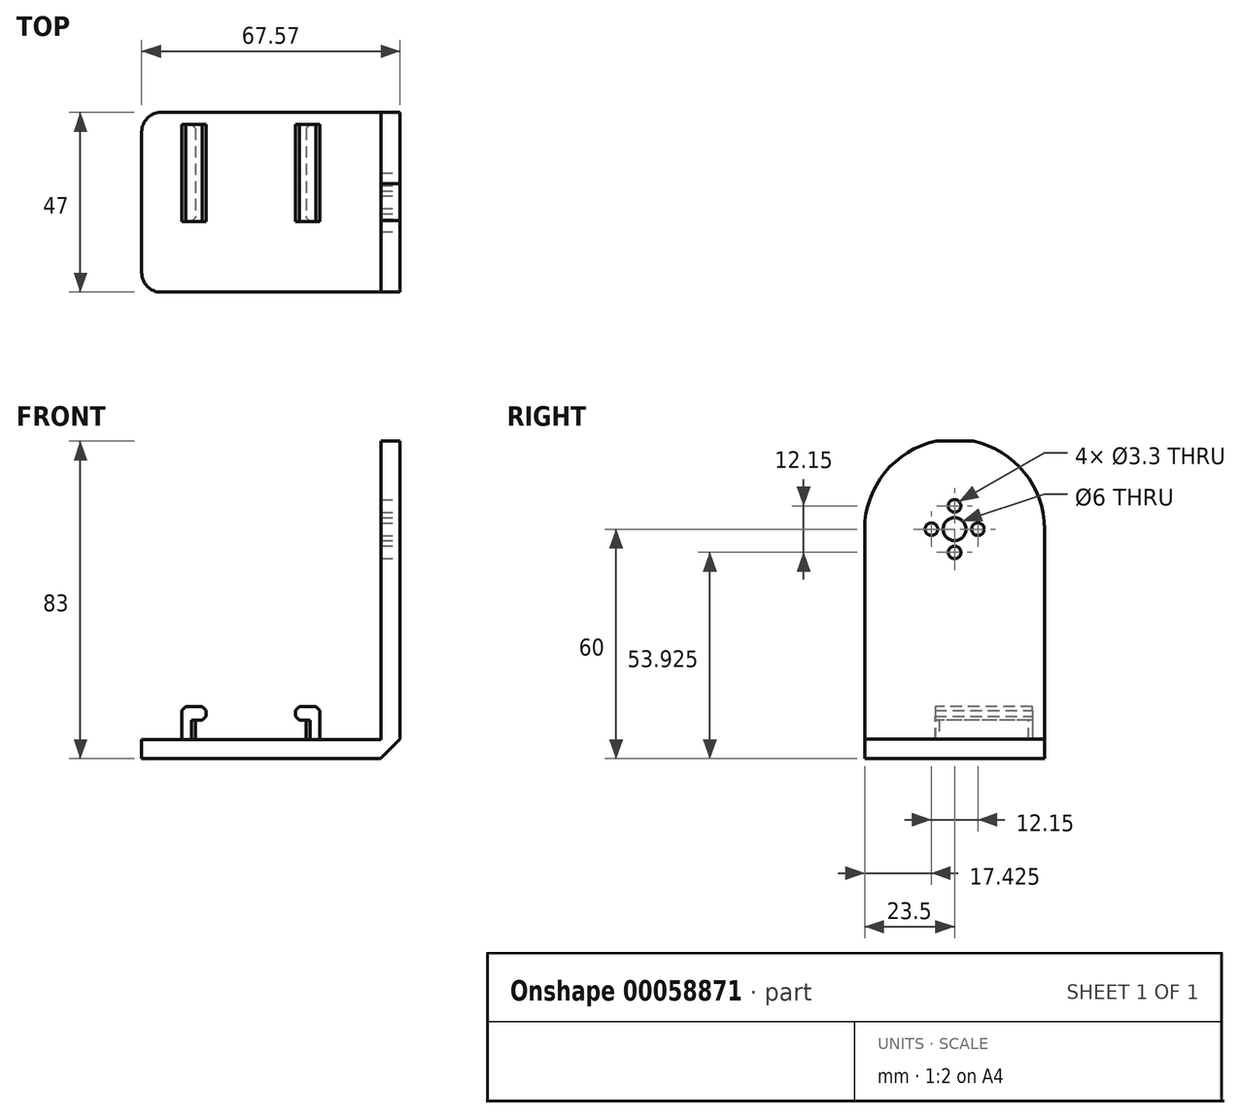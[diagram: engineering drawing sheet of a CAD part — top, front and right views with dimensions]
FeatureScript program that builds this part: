
annotation { "Feature Type Name" : "Feature", "Feature Type Description" : "" }
export const myFeature = defineFeature(function(context is Context, id is Id, definition is map)
    precondition{}
    {
        {
            var Q0;
            Q0=qCreatedBy(makeId("Top.planeOp"),FACE);
            var sketch = newSketch(context, id + "F0", { "sketchPlane" : qUnion([Q0])});
            skLineSegment(sketch, "E0.bottom", {"start": v(-28.58, 10.8) * mm, "end": v(28.58, 10.8) * mm});
            skLineSegment(sketch, "E0.top", {"start": v(-28.58, -10.8) * mm, "end": v(28.58, -10.8) * mm});
            skLineSegment(sketch, "E0.left", {"start": v(-28.57, 10.8) * mm, "end": v(-28.58, -10.8) * mm});
            skLineSegment(sketch, "E0.right", {"start": v(28.58, 10.8) * mm, "end": v(28.57, -10.8) * mm});
            skLineSegment(sketch, "E1", {"start": v(0, 10.8) * mm, "end": v(0, -10.8) * mm, "construction": true});
            skPoint(sketch, "E2", {"position": v(0, 0) * mm});
            skSolve(sketch);
        }
        {
            var Q0;
            Q0=qSketchRegion(id+"F0",true);
            extrude(context, id + "F1", {"entities" : qUnion([Q0]), "depth" : 5 * mm});
        }
        {
            var Q0;
            Q0=qCreatedBy(makeId("Top.planeOp"),FACE);
            var sketch = newSketch(context, id + "F2", { "sketchPlane" : qUnion([Q0])});
            skLineSegment(sketch, "E3.bottom", {"start": v(-28.57, 10.8) * mm, "end": v(28.58, 10.8) * mm});
            skLineSegment(sketch, "E3.top", {"start": v(-28.57, 36.2) * mm, "end": v(28.58, 36.2) * mm});
            skLineSegment(sketch, "E3.left", {"start": v(-28.57, 10.8) * mm, "end": v(-28.58, 36.2) * mm});
            skLineSegment(sketch, "E3.right", {"start": v(28.58, 10.8) * mm, "end": v(28.58, 36.2) * mm});
            skSolve(sketch);
        }
        {
            var Q0;
            Q0=qSketchRegion(id+"F2",true);
            extrude(context, id + "F3", {"entities" : qUnion([Q0]), "operationType" : NewBodyOperationType.ADD, "depth" : 5 * mm});
        }
        {
            var Q0;
            Q0=makeQuery(id+"F3.boolean.opBoolean","MERGE",FACE,{"derivedFrom":[makeQuery(id+"F1.opExtrude","CAP_FACE",FACE,{"disambiguationData":[OSD([sQuery(id+"F0.wireOp",EDGE,"E0.bottom"),sQuery(id+"F0.wireOp",EDGE,"E0.top"),sQuery(id+"F0.wireOp",EDGE,"E0.left"),sQuery(id+"F0.wireOp",EDGE,"E0.right"),sQuery(id+"F0.wireOp",EDGE,"28a9c39b-f770-489b-a02f-ce0b1f26b331"),sQuery(id+"F0.wireOp",EDGE,"4d5f723c-dec2-4723-b848-b3ff6702b9b40.MirrorC"),sQuery(id+"F0.wireOp",EDGE,"3c9fb506-c623-4861-a3c0-1a61a185bb210.MirrorC"),sQuery(id+"F0.wireOp",EDGE,"cd34c67d-a8e0-44d2-8d65-12e7f07ee4970.MirrorC")])],"isStart":false}),makeQuery(id+"F3.opExtrude","CAP_FACE",FACE,{"disambiguationData":[OSD([sQuery(id+"F2.wireOp",EDGE,"E3.bottom"),sQuery(id+"F2.wireOp",EDGE,"E3.top"),sQuery(id+"F2.wireOp",EDGE,"E3.left"),sQuery(id+"F2.wireOp",EDGE,"E3.right")])],"isStart":false})]});
            var sketch = newSketch(context, id + "F4", { "sketchPlane" : qUnion([Q0])});
            skLineSegment(sketch, "E4.bottom", {"start": v(-18.03, 33.02) * mm, "end": v(-14.48, 33.02) * mm});
            skLineSegment(sketch, "E4.top", {"start": v(-18.03, 7.62) * mm, "end": v(-14.48, 7.62) * mm});
            skLineSegment(sketch, "E4.left", {"start": v(-18.03, 33.02) * mm, "end": v(-18.03, 7.62) * mm});
            skLineSegment(sketch, "E4.right", {"start": v(-14.48, 33.02) * mm, "end": v(-14.48, 7.62) * mm});
            skLineSegment(sketch, "E5.MirrorCS", {"start": v(18.03, 7.62) * mm, "end": v(14.48, 7.62) * mm});
            skLineSegment(sketch, "E6.MirrorCS", {"start": v(14.48, 33.02) * mm, "end": v(14.48, 7.62) * mm});
            skLineSegment(sketch, "E7.MirrorCS", {"start": v(18.03, 33.02) * mm, "end": v(14.48, 33.02) * mm});
            skLineSegment(sketch, "E8.MirrorCS", {"start": v(18.03, 33.02) * mm, "end": v(18.03, 7.62) * mm});
            skLineSegment(sketch, "E9", {"start": v(-28.58, 12.7) * mm, "end": v(28.58, 12.7) * mm, "construction": true});
            skLineSegment(sketch, "E10", {"start": v(28.58, 20.32) * mm, "end": v(-28.57, 20.32) * mm, "construction": true});
            skPoint(sketch, "E11", {"position": v(-18.03, 20.32) * mm});
            skSolve(sketch);
        }
        {
            var Q0;
            Q0=qSketchRegion(id+"F4",true);
            extrude(context, id + "F5", {"entities" : qUnion([Q0]), "operationType" : NewBodyOperationType.ADD, "depth" : 5.08 * mm});
        }
        {
            var Q0;
            Q0=makeQuery(id+"F5.opExtrude","CAP_FACE",FACE,{"disambiguationData":[OSD([sQuery(id+"F4.wireOp",EDGE,"E4.bottom"),sQuery(id+"F4.wireOp",EDGE,"E4.top"),sQuery(id+"F4.wireOp",EDGE,"E4.left"),sQuery(id+"F4.wireOp",EDGE,"E4.right")])],"isStart":false});
            var sketch = newSketch(context, id + "F6", { "sketchPlane" : qUnion([Q0])});
            skLineSegment(sketch, "E12.bottom", {"start": v(-18.03, 33.02) * mm, "end": v(-11.68, 33.02) * mm});
            skLineSegment(sketch, "E12.top", {"start": v(-18.03, 7.62) * mm, "end": v(-11.68, 7.62) * mm});
            skLineSegment(sketch, "E12.left", {"start": v(-18.03, 33.02) * mm, "end": v(-18.03, 7.62) * mm});
            skLineSegment(sketch, "E12.right", {"start": v(-11.68, 33.02) * mm, "end": v(-11.68, 7.62) * mm});
            skLineSegment(sketch, "E13.bottom", {"start": v(18.03, 33.02) * mm, "end": v(11.68, 33.02) * mm});
            skLineSegment(sketch, "E13.top", {"start": v(18.03, 7.62) * mm, "end": v(11.68, 7.62) * mm});
            skLineSegment(sketch, "E13.left", {"start": v(18.03, 33.02) * mm, "end": v(18.03, 7.62) * mm});
            skLineSegment(sketch, "E13.right", {"start": v(11.68, 33.02) * mm, "end": v(11.68, 7.62) * mm});
            skSolve(sketch);
        }
        {
            var Q0;
            Q0=qSketchRegion(id+"F6",true);
            extrude(context, id + "F7", {"entities" : qUnion([Q0]), "operationType" : NewBodyOperationType.ADD, "depth" : 3.56 * mm});
        }
        {
            var Q0;
            Q0=makeQuery(id+"F7.opExtrude","CAP_EDGE",EDGE,{"disambiguationData":[OSD([sQuery(id+"F6.wireOp",EDGE,"E12.right")])],"isStart":false});
            var Q1;
            Q1=makeQuery(id+"F7.opExtrude","CAP_EDGE",EDGE,{"disambiguationData":[OSD([sQuery(id+"F6.wireOp",EDGE,"E12.right")])],"isStart":true});
            var Q2;
            Q2=makeQuery(id+"F7.opExtrude","CAP_EDGE",EDGE,{"disambiguationData":[OSD([sQuery(id+"F6.wireOp",EDGE,"E13.right")])],"isStart":false});
            var Q3;
            Q3=makeQuery(id+"F7.opExtrude","CAP_EDGE",EDGE,{"disambiguationData":[OSD([sQuery(id+"F6.wireOp",EDGE,"E13.right")])],"isStart":true});
            var Q4;
            Q4=makeQuery(id+"F7.opExtrude","CAP_EDGE",EDGE,{"disambiguationData":[OSD([sQuery(id+"F6.wireOp",EDGE,"E13.left")])],"isStart":false});
            var Q5;
            Q5=makeQuery(id+"F7.opExtrude","CAP_EDGE",EDGE,{"disambiguationData":[OSD([sQuery(id+"F6.wireOp",EDGE,"E12.left")])],"isStart":false});
            var Q6;
            Q6=makeQuery(id+"F5.opExtrude","CAP_EDGE",EDGE,{"disambiguationData":[OSD([sQuery(id+"F4.wireOp",EDGE,"E8.MirrorCS")])],"isStart":true});
            var Q7;
            Q7=makeQuery(id+"F5.opExtrude","CAP_EDGE",EDGE,{"disambiguationData":[OSD([sQuery(id+"F4.wireOp",EDGE,"E4.left")])],"isStart":true});
            var Q8;
            Q8=makeQuery(id+"F5.opExtrude","SWEPT_EDGE",EDGE,{"disambiguationData":[OSD([sQuery(id+"F4.wireOp",EDGE,"E6.MirrorCS"),sQuery(id+"F4.wireOp",EDGE,"E7.MirrorCS")])]});
            var Q9;
            Q9=makeQuery(id+"F5.opExtrude","SWEPT_EDGE",EDGE,{"disambiguationData":[OSD([sQuery(id+"F4.wireOp",EDGE,"E4.bottom"),sQuery(id+"F4.wireOp",EDGE,"E4.right")])]});
            var Q10;
            Q10=makeQuery(id+"F5.opExtrude","SWEPT_EDGE",EDGE,{"disambiguationData":[OSD([sQuery(id+"F4.wireOp",EDGE,"E4.top"),sQuery(id+"F4.wireOp",EDGE,"E4.right")])]});
            var Q11;
            Q11=makeQuery(id+"F5.opExtrude","SWEPT_EDGE",EDGE,{"disambiguationData":[OSD([sQuery(id+"F4.wireOp",EDGE,"E5.MirrorCS"),sQuery(id+"F4.wireOp",EDGE,"E6.MirrorCS")])]});
            chamfer(context, id + "F8", {"entities" : qUnion([Q0, Q1, Q2, Q3, Q4, Q5, Q6, Q7, Q8, Q9, Q10, Q11]), "width" : 1.02 * mm, "tangentPropagation" : true});
        }
        {
            var Q0;
            Q0=makeQuery(id+"F3.boolean.opBoolean","MERGE",FACE,{"derivedFrom":[makeQuery(id+"F1.opExtrude","CAP_FACE",FACE,{"disambiguationData":[OSD([sQuery(id+"F0.wireOp",EDGE,"E0.bottom"),sQuery(id+"F0.wireOp",EDGE,"E0.top"),sQuery(id+"F0.wireOp",EDGE,"E0.left"),sQuery(id+"F0.wireOp",EDGE,"E0.right")])],"isStart":false}),makeQuery(id+"F3.opExtrude","CAP_FACE",FACE,{"disambiguationData":[OSD([sQuery(id+"F2.wireOp",EDGE,"E3.bottom"),sQuery(id+"F2.wireOp",EDGE,"E3.top"),sQuery(id+"F2.wireOp",EDGE,"E3.left"),sQuery(id+"F2.wireOp",EDGE,"E3.right")])],"isStart":false})]});
            var sketch = newSketch(context, id + "F9", { "sketchPlane" : qUnion([Q0])});
            skLineSegment(sketch, "E14.bottom", {"start": v(28.58, -10.8) * mm, "end": v(39, -10.8) * mm});
            skLineSegment(sketch, "E14.top", {"start": v(28.58, 36.2) * mm, "end": v(39, 36.2) * mm});
            skLineSegment(sketch, "E14.left", {"start": v(28.57, -10.8) * mm, "end": v(28.57, 36.2) * mm});
            skLineSegment(sketch, "E14.right", {"start": v(39, -10.8) * mm, "end": v(39, 36.2) * mm});
            skLineSegment(sketch, "E15", {"start": v(0, -10.8) * mm, "end": v(0, 36.2) * mm, "construction": true});
            skSolve(sketch);
        }
        {
            var Q0;
            Q0 = qSketchRegion(id + "F9", true);
            extrude(context, id + "F10", {"entities" : qUnion([Q0]), "operationType" : NewBodyOperationType.ADD, "oppositeDirection" : true, "depth" : 5 * mm});
        }
        {
            var Q0;
            Q0=makeQuery(id+"F10.boolean.opBoolean","MERGE",FACE,{"derivedFrom":[makeQuery(id+"F3.boolean.opBoolean","MERGE",FACE,{"derivedFrom":[makeQuery(id+"F1.opExtrude","CAP_FACE",FACE,{"disambiguationData":[OSD([sQuery(id+"F0.wireOp",EDGE,"E0.bottom"),sQuery(id+"F0.wireOp",EDGE,"E0.top"),sQuery(id+"F0.wireOp",EDGE,"E0.left"),sQuery(id+"F0.wireOp",EDGE,"E0.right")])],"isStart":false}),makeQuery(id+"F3.opExtrude","CAP_FACE",FACE,{"disambiguationData":[OSD([sQuery(id+"F2.wireOp",EDGE,"E3.bottom"),sQuery(id+"F2.wireOp",EDGE,"E3.top"),sQuery(id+"F2.wireOp",EDGE,"E3.left"),sQuery(id+"F2.wireOp",EDGE,"E3.right")])],"isStart":false})]}),makeQuery(id+"F10.opExtrude","CAP_FACE",FACE,{"disambiguationData":[OSD([sQuery(id+"F9.wireOp",EDGE,"E14.bottom"),sQuery(id+"F9.wireOp",EDGE,"E14.top"),sQuery(id+"F9.wireOp",EDGE,"E14.left"),sQuery(id+"F9.wireOp",EDGE,"E14.right")])],"isStart":true})]});
            var sketch = newSketch(context, id + "F11", { "sketchPlane" : qUnion([Q0])});
            skLineSegment(sketch, "E16.bottom", {"start": v(39, -10.8) * mm, "end": v(34, -10.8) * mm});
            skLineSegment(sketch, "E16.top", {"start": v(39, 36.2) * mm, "end": v(34, 36.2) * mm});
            skLineSegment(sketch, "E16.left", {"start": v(39, -10.8) * mm, "end": v(39, 36.2) * mm});
            skLineSegment(sketch, "E16.right", {"start": v(34, -10.8) * mm, "end": v(34, 36.2) * mm});
            skSolve(sketch);
        }
        {
            var Q0;
            Q0 = qSketchRegion(id + "F11", true);
            extrude(context, id + "F12", {"entities" : qUnion([Q0]), "operationType" : NewBodyOperationType.ADD, "depth" : 78 * mm});
        }
        {
            var Q0;
            Q0=makeQuery(id+"F12.boolean.opBoolean","MERGE",FACE,{"derivedFrom":[makeQuery(id+"F10.opExtrude","SWEPT_FACE",FACE,{"disambiguationData":[OSD([sQuery(id+"F9.wireOp",EDGE,"E14.right")])]}),makeQuery(id+"F12.opExtrude","SWEPT_FACE",FACE,{"disambiguationData":[OSD([sQuery(id+"F11.wireOp",EDGE,"E16.left")])]})]});
            var sketch = newSketch(context, id + "F13", { "sketchPlane" : qUnion([Q0])});
            skLineSegment(sketch, "E17", {"start": v(12.7, 83) * mm, "end": v(12.7, 0) * mm, "construction": true});
            skLineSegment(sketch, "E18", {"start": v(-10.8, 60) * mm, "end": v(36.2, 60) * mm, "construction": true});
            skCircle(sketch, "E19", {"center": v(6.62, 60) * mm, "radius": 1.65 * mm});
            skCircle(sketch, "E20", {"center": v(12.7, 53.92) * mm, "radius": 1.65 * mm});
            skCircle(sketch, "E21.MirrorC", {"center": v(18.77, 60) * mm, "radius": 1.65 * mm});
            skCircle(sketch, "E22.MirrorC", {"center": v(12.7, 66.07) * mm, "radius": 1.65 * mm});
            skCircle(sketch, "E23", {"center": v(12.7, 60) * mm, "radius": 3 * mm});
            skSolve(sketch);
        }
        {
            var Q0;
            Q0 = qSketchRegion(id + "F13", true);
            extrude(context, id + "F14", {"entities" : qUnion([Q0]), "operationType" : NewBodyOperationType.REMOVE, "oppositeDirection" : true, "depth" : 25.4 * mm});
        }
        {
            var Q0;
            Q0=makeQuery(id+"F12.opExtrude","SWEPT_FACE",FACE,{"disambiguationData":[OSD([sQuery(id+"F11.wireOp",EDGE,"E16.right")])]});
            var sketch = newSketch(context, id + "F15", { "sketchPlane" : qUnion([Q0])});
            skArc(sketch, "E24", {"start": v(10.8, 60) * mm, "mid": v(-12.7, 83.5) * mm, "end": v(-36.2, 60) * mm});
            skLineSegment(sketch, "E25", {"start": v(-36.2, 60) * mm, "end": v(10.8, 60) * mm, "construction": true});
            skLineSegment(sketch, "E26", {"start": v(-36.2, 60) * mm, "end": v(-36.2, 83) * mm});
            skLineSegment(sketch, "E27", {"start": v(-36.2, 83) * mm, "end": v(10.8, 83) * mm});
            skLineSegment(sketch, "E28", {"start": v(10.8, 83) * mm, "end": v(10.8, 60) * mm});
            skSolve(sketch);
        }
        {
            var Q0;
            Q0 = qSketchRegion(id + "F15", true);
            extrude(context, id + "F16", {"entities" : qUnion([Q0]), "operationType" : NewBodyOperationType.REMOVE, "oppositeDirection" : true, "depth" : 25.4 * mm});
        }
        {
            var Q0;
            Q0=makeQuery(id+"F1.opExtrude","SWEPT_EDGE",EDGE,{"disambiguationData":[OSD([sQuery(id+"F0.wireOp",EDGE,"E0.top"),sQuery(id+"F0.wireOp",EDGE,"E0.left")])]});
            var Q1;
            Q1=makeQuery(id+"F3.opExtrude","SWEPT_EDGE",EDGE,{"disambiguationData":[OSD([sQuery(id+"F2.wireOp",EDGE,"E3.top"),sQuery(id+"F2.wireOp",EDGE,"E3.left")])]});
            fillet(context, id + "F17", {"entities" : qUnion([Q0, Q1]), "radius" : 5.08 * mm, "tangentPropagation" : true, "allowEdgeOverflow" : false});
        }
        {
            var Q0;
            Q0=makeQuery(id+"F12.opExtrude","CAP_EDGE",EDGE,{"disambiguationData":[OSD([sQuery(id+"F11.wireOp",EDGE,"E16.right")])],"isStart":true});
            var Q1;
            Q1=makeQuery(id+"F10.opExtrude","CAP_EDGE",EDGE,{"disambiguationData":[OSD([sQuery(id+"F9.wireOp",EDGE,"E14.right")])],"isStart":false});
            chamfer(context, id + "F18", {"entities" : qUnion([Q0, Q1]), "width" : 5.08 * mm, "tangentPropagation" : true});
        }
    });
